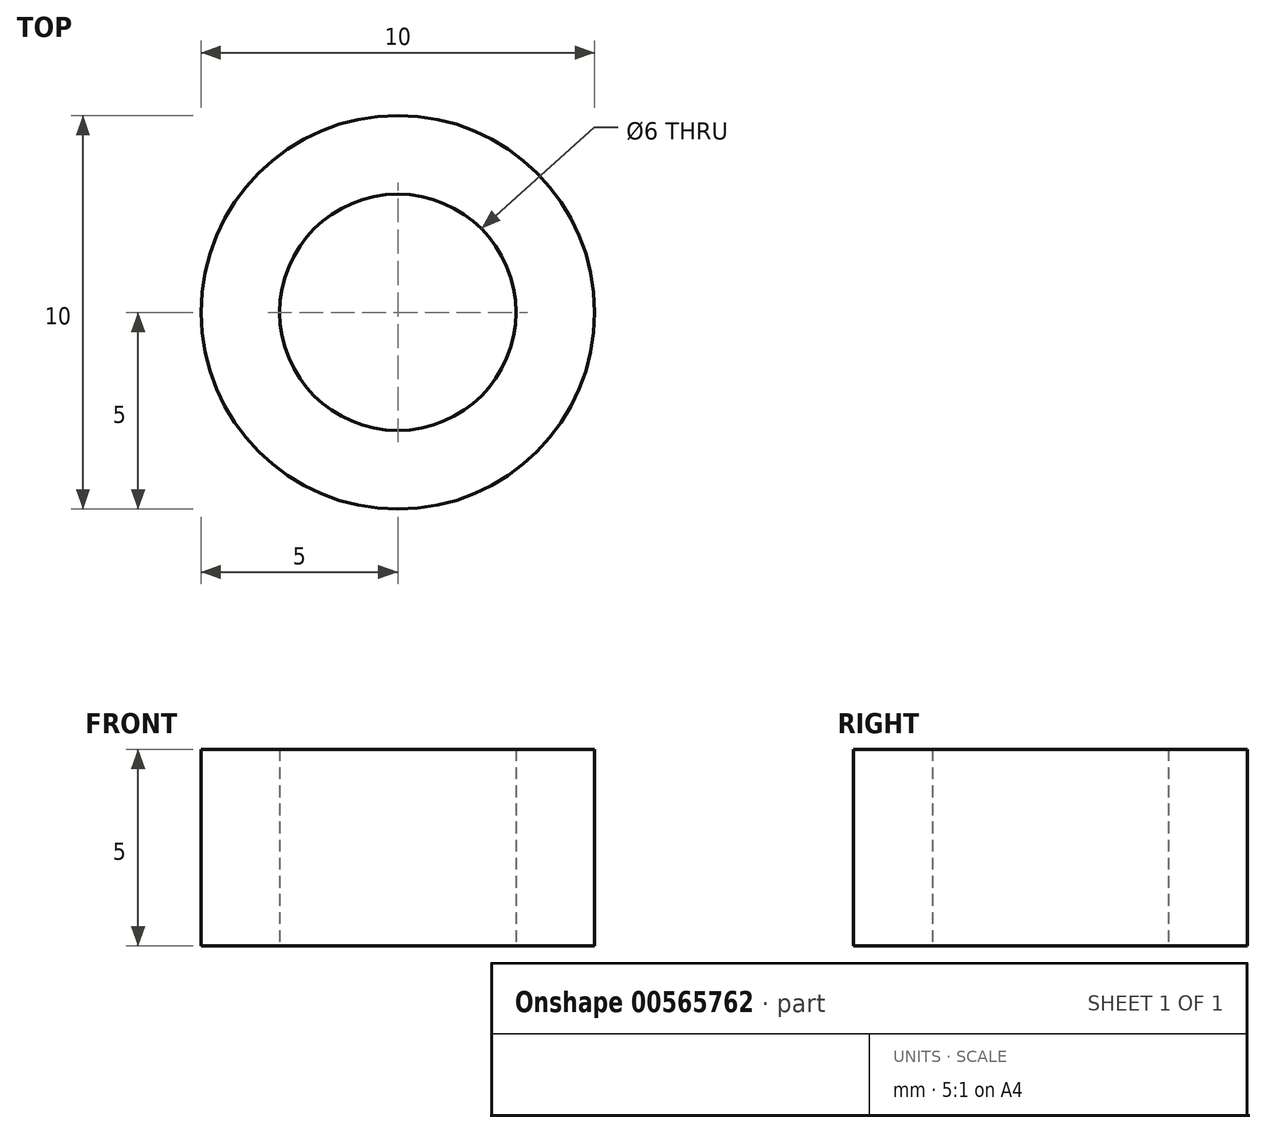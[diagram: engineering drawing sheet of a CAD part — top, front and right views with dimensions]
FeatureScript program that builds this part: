
annotation { "Feature Type Name" : "Feature", "Feature Type Description" : "" }
export const myFeature = defineFeature(function(context is Context, id is Id, definition is map)
    precondition{}
    {
        {
            var Q0;
            Q0=qCreatedBy(makeId("Top.planeOp"),FACE);
            var sketch = newSketch(context, id + "F0", { "sketchPlane" : qUnion([Q0])});
            skCircle(sketch, "E0", {"center": v(0, 0) * mm, "radius": 3 * mm});
            skCircle(sketch, "E1", {"center": v(0, 0) * mm, "radius": 5 * mm});
            skSolve(sketch);
        }
        {
            var Q0;
            Q0 = qSketchRegion(id + "F0", true);
            extrude(context, id + "F1", {"entities" : qUnion([Q0]), "depth" : 5 * mm, "offsetDistance" : 25 * mm});
        }
    });
